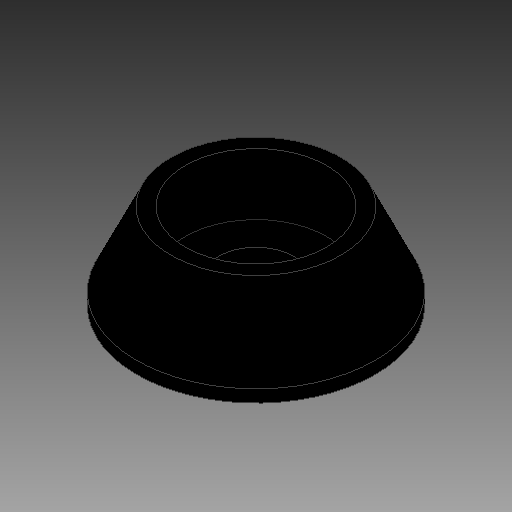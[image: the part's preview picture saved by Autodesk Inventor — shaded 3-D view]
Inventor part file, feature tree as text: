
AUTODESK INVENTOR PART (.ipt)
format: ipt  version: 2019 (Build 230136000, 136)  size: 102,400 bytes
history: native  units: mm
features: revolve x1, sketch x1
ambient origin geometry x8: Origin, YZ Plane, XZ Plane, XY Plane, X Axis, Y Axis, Z Axis, Center Point
bodies: Solid1 (feature_tree)
feature tree (2):
  revolve  "Revolution1"  [1 undecoded]
  sketch  "Sketch1"  dims[d0=2.875mm d1=1.5mm d2=1.0mm d3=3.45mm d4=3.5mm d5=4.85mm d6=0.5mm d7=90.0deg]
note: 1 required parameter value undecoded (feature->parameter linkage not recoverable at this tier; creation-order binding heuristic only, values carry confidence <= 0.55)
